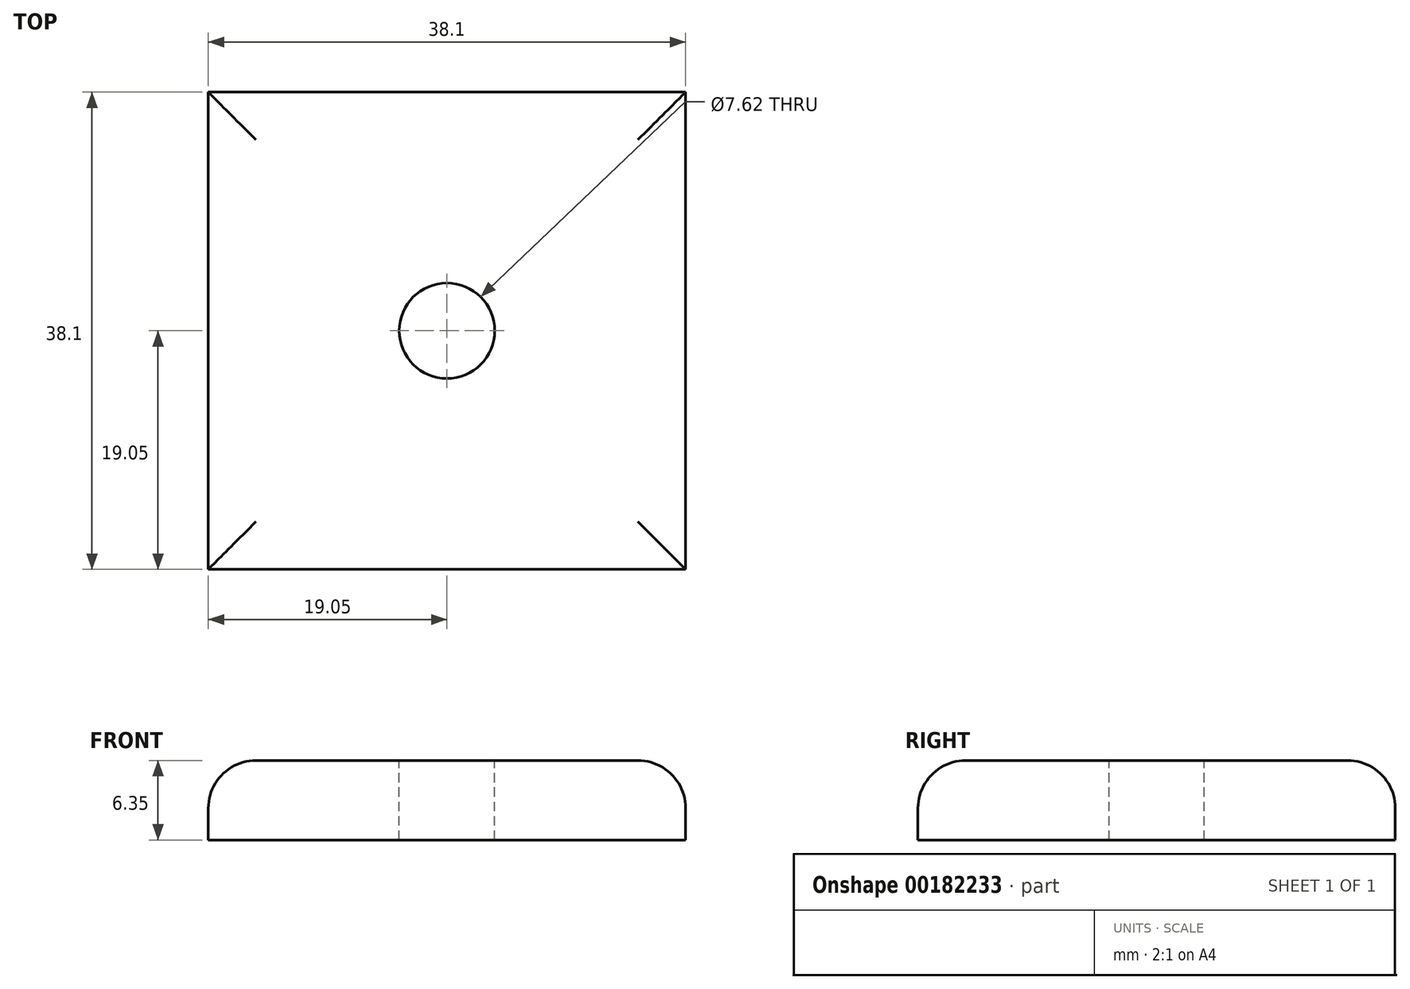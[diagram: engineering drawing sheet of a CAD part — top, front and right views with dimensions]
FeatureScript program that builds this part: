
annotation { "Feature Type Name" : "Feature", "Feature Type Description" : "" }
export const myFeature = defineFeature(function(context is Context, id is Id, definition is map)
    precondition{}
    {
        {
            var Q0;
            Q0=qCreatedBy(makeId("Top.planeOp"),FACE);
            var sketch = newSketch(context, id + "F0", { "sketchPlane" : qUnion([Q0])});
            skLineSegment(sketch, "E0.bottom", {"start": v(0, 0) * mm, "end": v(38.1, 0) * mm});
            skLineSegment(sketch, "E0.top", {"start": v(0, 38.1) * mm, "end": v(38.1, 38.1) * mm});
            skLineSegment(sketch, "E0.left", {"start": v(0, 0) * mm, "end": v(0, 38.1) * mm});
            skLineSegment(sketch, "E0.right", {"start": v(38.1, 0) * mm, "end": v(38.1, 38.1) * mm});
            skSolve(sketch);
        }
        {
            var Q0;
            Q0=qSketchRegion(id+"F0",true);
            extrude(context, id + "F1", {"entities" : qUnion([Q0]), "oppositeDirection" : true, "depth" : 6.35 * mm});
        }
        {
            var Q0;
            Q0=makeQuery(id+"F1.opExtrude","CAP_EDGE",EDGE,{"disambiguationData":[OSD([sQuery(id+"F0.wireOp",EDGE,"E0.left")])],"isStart":true});
            var Q1;
            Q1=makeQuery(id+"F1.opExtrude","CAP_EDGE",EDGE,{"disambiguationData":[OSD([sQuery(id+"F0.wireOp",EDGE,"E0.bottom")])],"isStart":true});
            var Q2;
            Q2=makeQuery(id+"F1.opExtrude","CAP_EDGE",EDGE,{"disambiguationData":[OSD([sQuery(id+"F0.wireOp",EDGE,"E0.right")])],"isStart":true});
            var Q3;
            Q3=makeQuery(id+"F1.opExtrude","CAP_EDGE",EDGE,{"disambiguationData":[OSD([sQuery(id+"F0.wireOp",EDGE,"E0.top")])],"isStart":true});
            fillet(context, id + "F2", {"entities" : qUnion([Q0, Q1, Q2, Q3]), "radius" : 3.8 * mm, "tangentPropagation" : true, "allowEdgeOverflow" : false});
        }
        {
            var Q0;
            Q0=makeQuery(id+"F1.opExtrude","CAP_FACE",FACE,{"disambiguationData":[OSD([sQuery(id+"F0.wireOp",EDGE,"E0.bottom"),sQuery(id+"F0.wireOp",EDGE,"E0.top"),sQuery(id+"F0.wireOp",EDGE,"E0.left"),sQuery(id+"F0.wireOp",EDGE,"E0.right")])],"isStart":true});
            var sketch = newSketch(context, id + "F3", { "sketchPlane" : qUnion([Q0])});
            skCircle(sketch, "E1", {"center": v(19.05, 19.05) * mm, "radius": 3.8 * mm});
            skSolve(sketch);
        }
        {
            var Q0;
            Q0=qSketchRegion(id+"F3",true);
            extrude(context, id + "F4", {"entities" : qUnion([Q0]), "operationType" : NewBodyOperationType.REMOVE, "endBound" : BoundingType.THROUGH_ALL, "oppositeDirection" : true, "depth" : 25.4 * mm});
        }
    });
